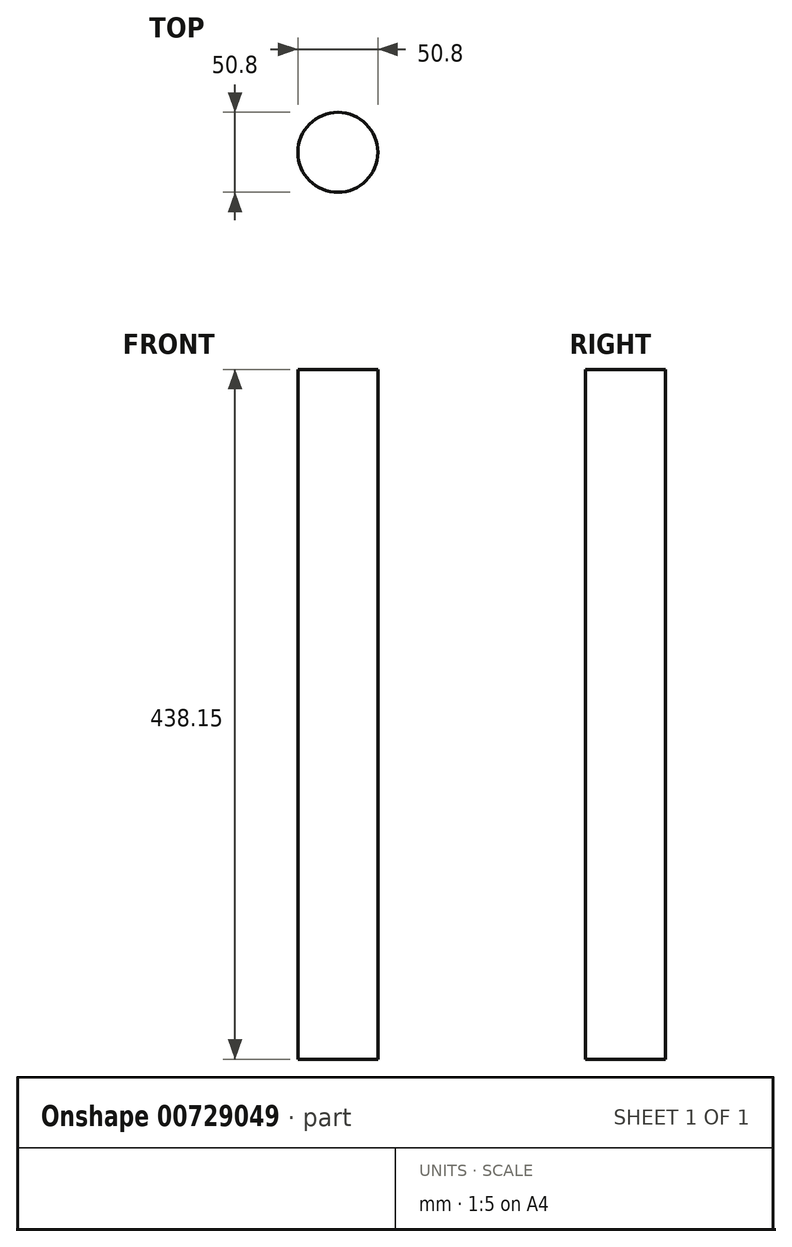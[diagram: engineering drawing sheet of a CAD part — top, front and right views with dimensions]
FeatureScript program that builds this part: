
annotation { "Feature Type Name" : "Feature", "Feature Type Description" : "" }
export const myFeature = defineFeature(function(context is Context, id is Id, definition is map)
    precondition{}
    {
        {
            var Q0;
            Q0=qCreatedBy(makeId("Top.planeOp"),FACE);
            var sketch = newSketch(context, id + "F0", { "sketchPlane" : qUnion([Q0])});
            skCircle(sketch, "E0", {"center": v(0, 0) * mm, "radius": 25.4 * mm});
            skSolve(sketch);
        }
        {
            var Q0;
            Q0 = qSketchRegion(id + "F0", true);
            extrude(context, id + "F1", {"entities" : qUnion([Q0]), "depth" : 438.15 * mm, "offsetDistance" : 25.4 * mm});
        }
    });
